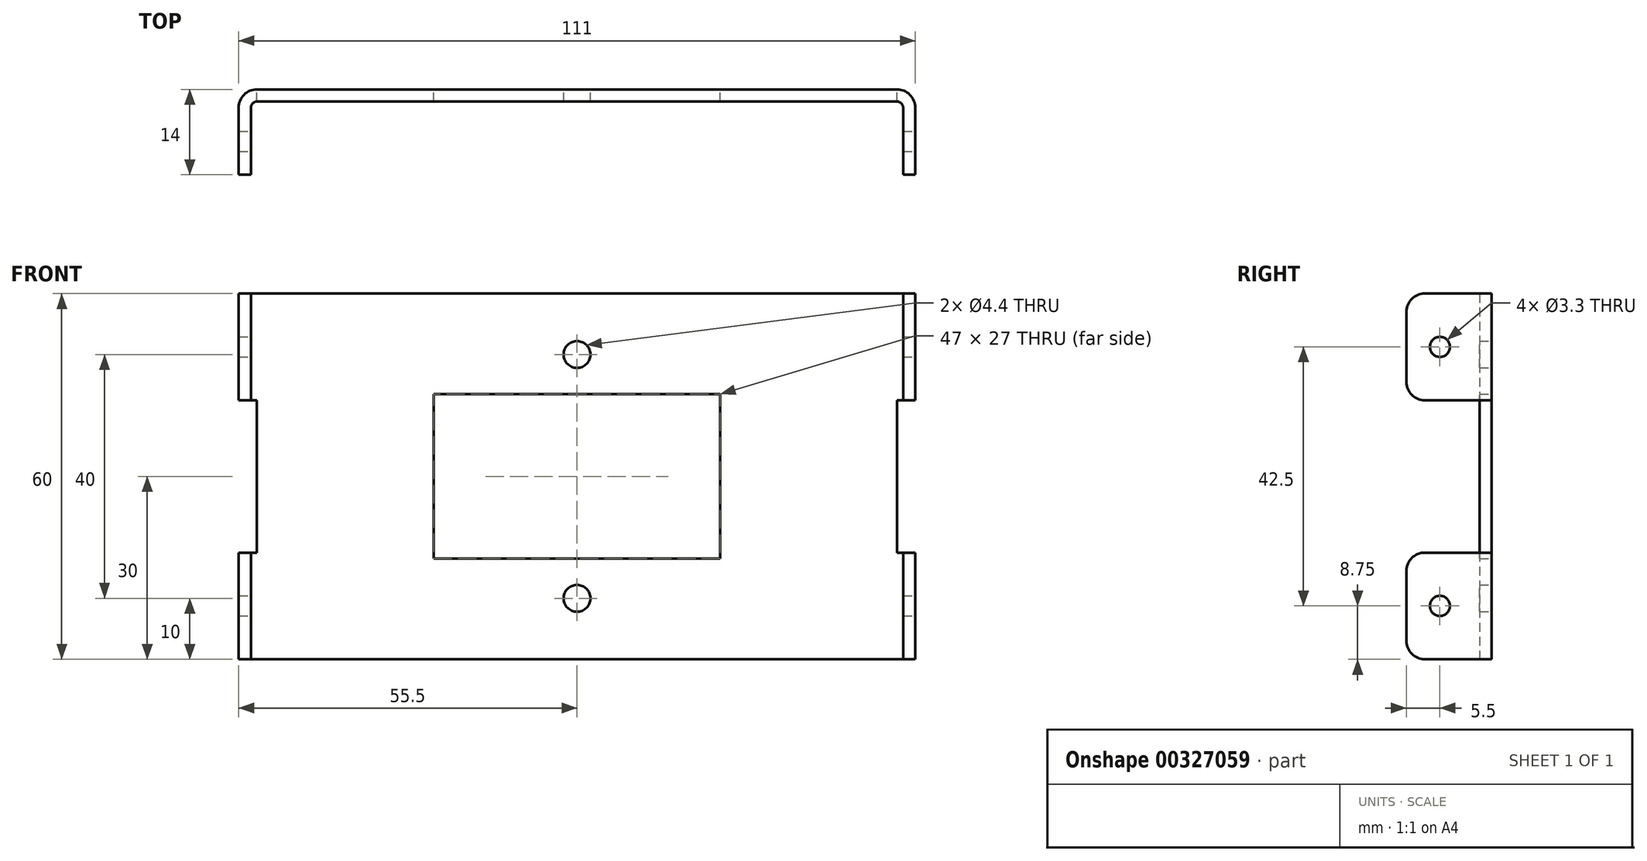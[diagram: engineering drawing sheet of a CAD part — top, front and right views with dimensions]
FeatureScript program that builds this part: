
annotation { "Feature Type Name" : "Feature", "Feature Type Description" : "" }
export const myFeature = defineFeature(function(context is Context, id is Id, definition is map)
    precondition{}
    {
        {
            var Q0;
            Q0=qCreatedBy(makeId("Top.planeOp"),FACE);
            var sketch = newSketch(context, id + "F0", { "sketchPlane" : qUnion([Q0])});
            skLineSegment(sketch, "E0", {"start": v(52.5, 0) * mm, "end": v(-52.5, 0) * mm});
            skLineSegment(sketch, "E1", {"start": v(-53.5, -1) * mm, "end": v(-53.5, -12) * mm});
            skLineSegment(sketch, "E2", {"start": v(53.5, -1) * mm, "end": v(53.5, -12) * mm});
            skPoint(sketch, "E3", {"position": v(0, 0) * mm});
            skPoint(sketch, "E4.visualSharp", {"position": v(-53.5, 0) * mm});
            skArc(sketch, "E4.filletArc", {"start": v(-52.5, 0) * mm, "mid": v(-53.2, -0.3) * mm, "end": v(-53.5, -1) * mm});
            skPoint(sketch, "E5.visualSharp", {"position": v(53.5, 0) * mm});
            skArc(sketch, "E5.filletArc", {"start": v(53.5, -1) * mm, "mid": v(53.2, -0.3) * mm, "end": v(52.5, 0) * mm});
            skLineSegment(sketch, "E6.0", {"start": v(-55.5, -1) * mm, "end": v(-55.5, -12) * mm});
            skLineSegment(sketch, "E6.1", {"start": v(55.5, -1) * mm, "end": v(55.5, -12) * mm});
            skArc(sketch, "E6.2", {"start": v(55.5, -1) * mm, "mid": v(54.62, 1.12) * mm, "end": v(52.5, 2) * mm});
            skLineSegment(sketch, "E6.3", {"start": v(52.5, 2) * mm, "end": v(-52.5, 2) * mm});
            skArc(sketch, "E6.4", {"start": v(-52.5, 2) * mm, "mid": v(-54.62, 1.12) * mm, "end": v(-55.5, -1) * mm});
            skLineSegment(sketch, "E7", {"start": v(-55.5, -12) * mm, "end": v(-53.5, -12) * mm});
            skLineSegment(sketch, "E8", {"start": v(53.5, -12) * mm, "end": v(55.5, -12) * mm});
            skSolve(sketch);
        }
        {
            var Q0;
            Q0=makeQuery(id+"F0.imprint","IMPRINT",FACE,{"disambiguationData":[TD([[makeQuery(id+"F0.imprint","IMPRINT",EDGE,{"derivedFrom":sQuery(id+"F0.wireOp",EDGE,"E0")}),-1.0]])]});
            extrude(context, id + "F1", {"entities" : qUnion([Q0]), "depth" : 60 * mm, "symmetric" : true});
        }
        {
            var Q0;
            Q0=makeQuery(id+"F1.opExtrude","SWEPT_FACE",FACE,{"disambiguationData":[OSD([sQuery(id+"F0.wireOp",EDGE,"E6.3")])]});
            var sketch = newSketch(context, id + "F2", { "sketchPlane" : qUnion([Q0])});
            skLineSegment(sketch, "E9.0", {"start": v(-55.5, 30) * mm, "end": v(-55.5, -30) * mm, "construction": true});
            skLineSegment(sketch, "E10.0", {"start": v(55.5, 30) * mm, "end": v(55.5, -30) * mm, "construction": true});
            skLineSegment(sketch, "E11.bottom", {"start": v(-55.5, 12.5) * mm, "end": v(-52.5, 12.5) * mm});
            skLineSegment(sketch, "E11.top", {"start": v(-55.5, -12.5) * mm, "end": v(-52.5, -12.5) * mm});
            skLineSegment(sketch, "E11.left", {"start": v(-55.5, 12.5) * mm, "end": v(-55.5, -12.5) * mm});
            skLineSegment(sketch, "E11.right", {"start": v(-52.5, 12.5) * mm, "end": v(-52.5, -12.5) * mm});
            skPoint(sketch, "E12", {"position": v(-52.5, 0) * mm});
            skLineSegment(sketch, "E13", {"start": v(0, 0) * mm, "end": v(0, 30) * mm, "construction": true});
            skLineSegment(sketch, "E14.MirrorCS", {"start": v(55.5, 12.5) * mm, "end": v(52.5, 12.5) * mm});
            skLineSegment(sketch, "E15.MirrorCS", {"start": v(55.5, -12.5) * mm, "end": v(52.5, -12.5) * mm});
            skPoint(sketch, "E16.MirrorP", {"position": v(52.5, 0) * mm});
            skLineSegment(sketch, "E17.MirrorCS", {"start": v(55.5, 12.5) * mm, "end": v(55.5, -12.5) * mm});
            skLineSegment(sketch, "E18.MirrorCS", {"start": v(52.5, 12.5) * mm, "end": v(52.5, -12.5) * mm});
            skLineSegment(sketch, "E19.bottom", {"start": v(23.5, 13.5) * mm, "end": v(-23.5, 13.5) * mm});
            skLineSegment(sketch, "E19.top", {"start": v(23.5, -13.5) * mm, "end": v(-23.5, -13.5) * mm});
            skLineSegment(sketch, "E19.left", {"start": v(23.5, 13.5) * mm, "end": v(23.5, -13.5) * mm});
            skLineSegment(sketch, "E19.right", {"start": v(-23.5, 13.5) * mm, "end": v(-23.5, -13.5) * mm});
            skPoint(sketch, "E19.middle", {"position": v(0, 0) * mm});
            skPoint(sketch, "E20", {"position": v(0, 20) * mm});
            skLineSegment(sketch, "E21", {"start": v(0, 0) * mm, "end": v(23.5, 0) * mm, "construction": true});
            skPoint(sketch, "E22", {"position": v(0, -20) * mm});
            skSolve(sketch);
        }
        {
            var Q0;
            Q0=makeQuery(id+"F2.imprint","IMPRINT",FACE,{"disambiguationData":[TD([[makeQuery(id+"F2.imprint","IMPRINT",EDGE,{"derivedFrom":sQuery(id+"F2.wireOp",EDGE,"E11.bottom")}),-1.0]])]});
            var Q1;
            Q1=makeQuery(id+"F2.imprint","IMPRINT",FACE,{"disambiguationData":[TD([[makeQuery(id+"F2.imprint","IMPRINT",EDGE,{"derivedFrom":sQuery(id+"F2.wireOp",EDGE,"E14.MirrorCS")}),1.0]])]});
            var Q2;
            Q2=makeQuery(id+"F2.imprint","IMPRINT",FACE,{"disambiguationData":[TD([[makeQuery(id+"F2.imprint","IMPRINT",EDGE,{"derivedFrom":sQuery(id+"F2.wireOp",EDGE,"E19.bottom")}),1.0]])]});
            extrude(context, id + "F3", {"entities" : qUnion([Q0, Q1, Q2]), "operationType" : NewBodyOperationType.REMOVE, "endBound" : BoundingType.THROUGH_ALL, "oppositeDirection" : true, "depth" : 25 * mm});
        }
        {
            var Q0;
            Q0=sQuery(id+"F2.wireOp",VERTEX,"E20");
            var Q1;
            Q1=sQuery(id+"F2.wireOp",VERTEX,"E22");
            var Q2;
            Q2=makeQuery(id+"F1.opExtrude","SWEPT_BODY",BODY,{"disambiguationData":[OSD([sQuery(id+"F0.wireOp",EDGE,"E0"),sQuery(id+"F0.wireOp",EDGE,"E1"),sQuery(id+"F0.wireOp",EDGE,"E2"),sQuery(id+"F0.wireOp",EDGE,"E4.filletArc"),sQuery(id+"F0.wireOp",EDGE,"E5.filletArc"),sQuery(id+"F0.wireOp",EDGE,"E6.0"),sQuery(id+"F0.wireOp",EDGE,"E6.1"),sQuery(id+"F0.wireOp",EDGE,"E6.2"),sQuery(id+"F0.wireOp",EDGE,"E6.3"),sQuery(id+"F0.wireOp",EDGE,"E6.4"),sQuery(id+"F0.wireOp",EDGE,"E7"),sQuery(id+"F0.wireOp",EDGE,"E8")])]});
            hole(context, id + "F4", {"style" : HoleStyle.SIMPLE, "endStyle" : HoleEndStyle.THROUGH, "standardTappedOrClearance" : lookupTablePath({ "standard" : "ISO", "fit" : "Normal", "size" : "M4", "type" : "Clearance" }), "standardBlindInLast" : lookupTablePath({ "fit" : "Standard", "standard" : "ISO", "size" : "M4", "type" : "Clearance" }), "holeDiameter" : 4.4 * mm, "tappedDepth" : 12 * mm, "tapClearance" : 3, "locations" : qUnion([Q0, Q1]), "scope" : qUnion([Q2])});
        }
        {
            var Q0;
            {var subQ2=sQuery(id+"F0.wireOp",EDGE,"E6.1");Q0=makeQuery(id+"F3.boolean.opBoolean","SPLIT",FACE,{"disambiguationData":[TD([makeQuery(id+"F3.opExtrude","SWEPT_FACE",FACE,{"disambiguationData":[OSD([sQuery(id+"F2.wireOp",EDGE,"E11.bottom")])]})])],"derivedFrom":makeQuery(id+"F1.opExtrude","SWEPT_FACE",FACE,{"disambiguationData":[OSD([subQ2])]})});}
            var sketch = newSketch(context, id + "F5", { "sketchPlane" : qUnion([Q0])});
            skLineSegment(sketch, "E23", {"start": v(-1, 12.5) * mm, "end": v(-12, 30) * mm, "construction": true});
            skLineSegment(sketch, "E24.0.0", {"start": v(-1, -12.5) * mm, "end": v(-12, -12.5) * mm, "construction": true});
            skLineSegment(sketch, "E24.0.1", {"start": v(-12, -12.5) * mm, "end": v(-12, -30) * mm, "construction": true});
            skLineSegment(sketch, "E24.0.2", {"start": v(-12, -30) * mm, "end": v(-1, -30) * mm, "construction": true});
            skLineSegment(sketch, "E24.0.3", {"start": v(-1, -30) * mm, "end": v(-1, -12.5) * mm, "construction": true});
            skLineSegment(sketch, "E25", {"start": v(-1, -30) * mm, "end": v(-12, -12.5) * mm, "construction": true});
            skPoint(sketch, "E26", {"position": v(-6.5, 21.25) * mm});
            skPoint(sketch, "E27", {"position": v(-6.5, -21.25) * mm});
            skSolve(sketch);
        }
        {
            var Q0;
            Q0=sQuery(id+"F5.wireOp",VERTEX,"E26");
            var Q1;
            Q1=sQuery(id+"F5.wireOp",VERTEX,"E27");
            var Q2;
            Q2=makeQuery(id+"F1.opExtrude","SWEPT_BODY",BODY,{"disambiguationData":[OSD([sQuery(id+"F0.wireOp",EDGE,"E0"),sQuery(id+"F0.wireOp",EDGE,"E1"),sQuery(id+"F0.wireOp",EDGE,"E2"),sQuery(id+"F0.wireOp",EDGE,"E4.filletArc"),sQuery(id+"F0.wireOp",EDGE,"E5.filletArc"),sQuery(id+"F0.wireOp",EDGE,"E6.0"),sQuery(id+"F0.wireOp",EDGE,"E6.1"),sQuery(id+"F0.wireOp",EDGE,"E6.2"),sQuery(id+"F0.wireOp",EDGE,"E6.3"),sQuery(id+"F0.wireOp",EDGE,"E6.4"),sQuery(id+"F0.wireOp",EDGE,"E7"),sQuery(id+"F0.wireOp",EDGE,"E8")])]});
            hole(context, id + "F6", {"style" : HoleStyle.SIMPLE, "endStyle" : HoleEndStyle.THROUGH, "standardTappedOrClearance" : lookupTablePath({ "standard" : "ISO", "fit" : "Normal", "size" : "M3", "type" : "Clearance" }), "standardBlindInLast" : lookupTablePath({ "fit" : "Standard", "standard" : "ISO", "size" : "M3", "type" : "Clearance" }), "holeDiameter" : 3.3 * mm, "tappedDepth" : 12 * mm, "tapClearance" : 3, "locations" : qUnion([Q0, Q1]), "scope" : qUnion([Q2])});
        }
        {
            var Q0;
            Q0=makeQuery(id+"F1.opExtrude","CAP_EDGE",EDGE,{"disambiguationData":[OSD([sQuery(id+"F0.wireOp",EDGE,"E7")])],"isStart":false});
            var Q1;
            Q1=makeQuery(id+"F3.boolean.opBoolean","INTERSECT",EDGE,{"derivedFrom":[makeQuery(id+"F1.opExtrude","SWEPT_FACE",FACE,{"disambiguationData":[OSD([sQuery(id+"F0.wireOp",EDGE,"E7")])]}),makeQuery(id+"F3.opExtrude","SWEPT_FACE",FACE,{"disambiguationData":[OSD([sQuery(id+"F2.wireOp",EDGE,"E14.MirrorCS")])]})]});
            var Q2;
            Q2=makeQuery(id+"F3.boolean.opBoolean","INTERSECT",EDGE,{"derivedFrom":[makeQuery(id+"F1.opExtrude","SWEPT_FACE",FACE,{"disambiguationData":[OSD([sQuery(id+"F0.wireOp",EDGE,"E7")])]}),makeQuery(id+"F3.opExtrude","SWEPT_FACE",FACE,{"disambiguationData":[OSD([sQuery(id+"F2.wireOp",EDGE,"E15.MirrorCS")])]})]});
            var Q3;
            Q3=makeQuery(id+"F1.opExtrude","CAP_EDGE",EDGE,{"disambiguationData":[OSD([sQuery(id+"F0.wireOp",EDGE,"E7")])],"isStart":true});
            var Q4;
            Q4=makeQuery(id+"F1.opExtrude","CAP_EDGE",EDGE,{"disambiguationData":[OSD([sQuery(id+"F0.wireOp",EDGE,"E8")])],"isStart":false});
            var Q5;
            Q5=makeQuery(id+"F3.boolean.opBoolean","INTERSECT",EDGE,{"derivedFrom":[makeQuery(id+"F1.opExtrude","SWEPT_FACE",FACE,{"disambiguationData":[OSD([sQuery(id+"F0.wireOp",EDGE,"E8")])]}),makeQuery(id+"F3.opExtrude","SWEPT_FACE",FACE,{"disambiguationData":[OSD([sQuery(id+"F2.wireOp",EDGE,"E11.bottom")])]})]});
            var Q6;
            Q6=makeQuery(id+"F3.boolean.opBoolean","INTERSECT",EDGE,{"derivedFrom":[makeQuery(id+"F1.opExtrude","SWEPT_FACE",FACE,{"disambiguationData":[OSD([sQuery(id+"F0.wireOp",EDGE,"E8")])]}),makeQuery(id+"F3.opExtrude","SWEPT_FACE",FACE,{"disambiguationData":[OSD([sQuery(id+"F2.wireOp",EDGE,"E11.top")])]})]});
            var Q7;
            Q7=makeQuery(id+"F1.opExtrude","CAP_EDGE",EDGE,{"disambiguationData":[OSD([sQuery(id+"F0.wireOp",EDGE,"E8")])],"isStart":true});
            fillet(context, id + "F7", {"entities" : qUnion([Q0, Q1, Q2, Q3, Q4, Q5, Q6, Q7]), "radius" : 3 * mm, "tangentPropagation" : true, "allowEdgeOverflow" : false});
        }
    });
